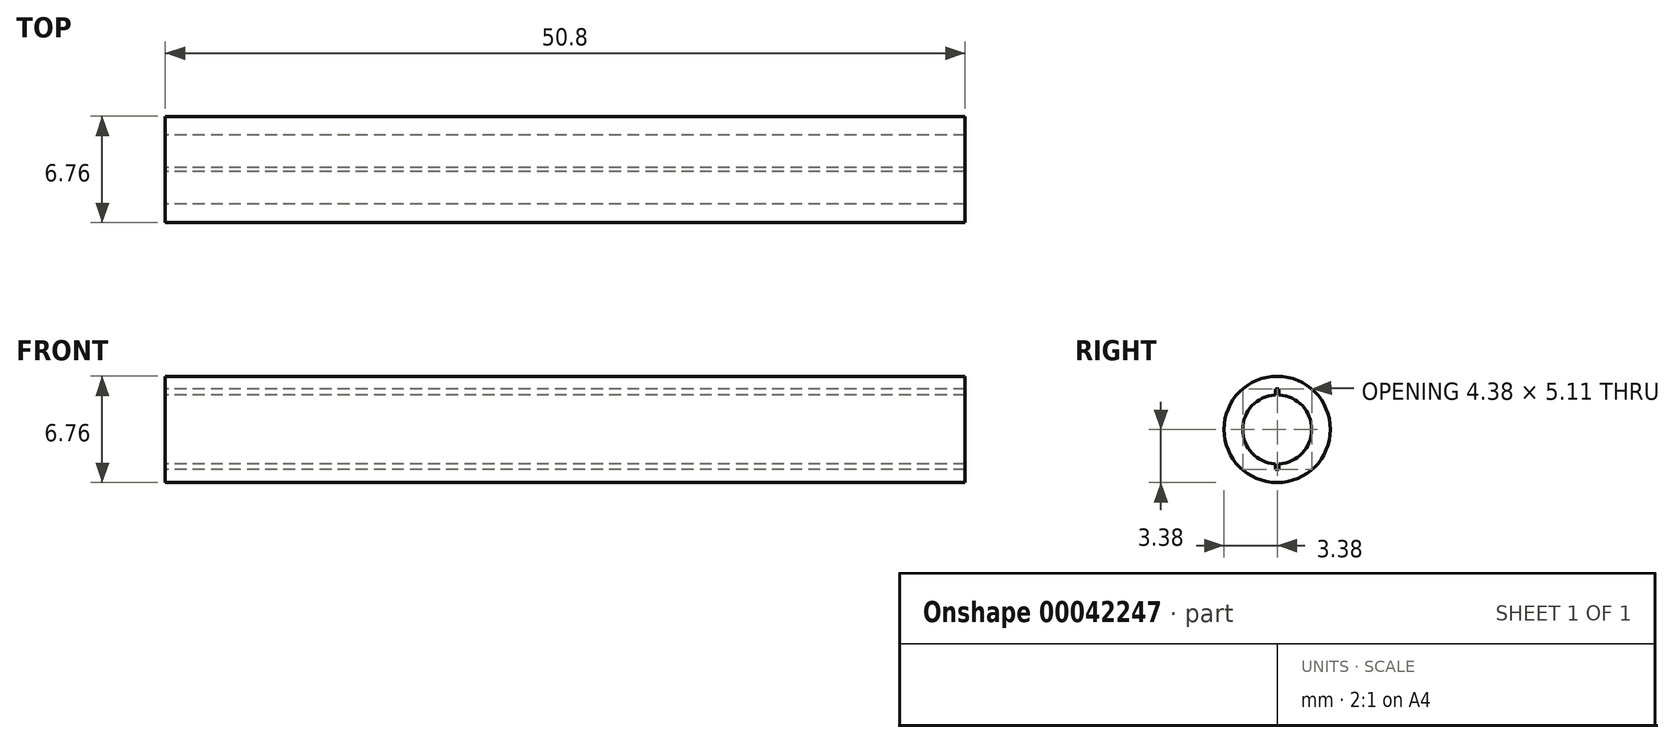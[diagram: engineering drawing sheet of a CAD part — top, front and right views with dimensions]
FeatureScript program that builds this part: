
annotation { "Feature Type Name" : "Feature", "Feature Type Description" : "" }
export const myFeature = defineFeature(function(context is Context, id is Id, definition is map)
    precondition{}
    {
        {
            var Q0;
            Q0=qCreatedBy(makeId("Right.planeOp"),FACE);
            var sketch = newSketch(context, id + "F0", { "sketchPlane" : qUnion([Q0])});
            skCircle(sketch, "E0", {"center": v(0, 0) * mm, "radius": 2.2 * mm});
            skCircle(sketch, "E1", {"center": v(0, 0) * mm, "radius": 3.38 * mm});
            skLineSegment(sketch, "E2", {"start": v(-0.12, 0) * mm, "end": v(-0.12, 2.56) * mm});
            skLineSegment(sketch, "E3", {"start": v(-0.12, 2.56) * mm, "end": v(0, 2.56) * mm});
            skLineSegment(sketch, "E4", {"start": v(0, 2.56) * mm, "end": v(0, 0) * mm});
            skLineSegment(sketch, "E5.MirrorCS", {"start": v(0.12, 0) * mm, "end": v(0.12, 2.56) * mm});
            skLineSegment(sketch, "E6.MirrorCS", {"start": v(0.12, 2.56) * mm, "end": v(0, 2.56) * mm});
            skLineSegment(sketch, "E7.MirrorCS", {"start": v(0.12, 0) * mm, "end": v(0.12, -2.56) * mm});
            skLineSegment(sketch, "E8.MirrorCS", {"start": v(-0.12, 0) * mm, "end": v(-0.12, -2.56) * mm});
            skLineSegment(sketch, "E9.MirrorCS", {"start": v(-0.12, -2.56) * mm, "end": v(0, -2.56) * mm});
            skLineSegment(sketch, "E10.MirrorCS", {"start": v(0.12, -2.56) * mm, "end": v(0, -2.56) * mm});
            skSolve(sketch);
        }
        {
            var Q0;
            Q0=makeQuery(id+"F0.imprint","IMPRINT",FACE,{"disambiguationData":[TD([[makeQuery(id+"F0.imprint","IMPRINT",EDGE,{"derivedFrom":sQuery(id+"F0.wireOp",EDGE,"E1")}),1.0]])]});
            extrude(context, id + "F1", {"entities" : qUnion([Q0]), "depth" : 50.8 * mm});
        }
    });
